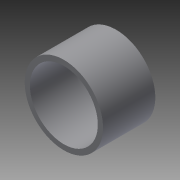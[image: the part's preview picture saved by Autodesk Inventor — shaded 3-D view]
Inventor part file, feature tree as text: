
AUTODESK INVENTOR PART (.ipt)
format: ipt  version: 2015 (Build 190159000, 159)  size: 107,008 bytes
history: native  units: mm
features: extrude x2, sketch x2
ambient origin geometry x8: Origin, YZ Plane, XZ Plane, XY Plane, X Axis, Y Axis, Z Axis, Center Point
bodies: Solid1 (feature_tree)
feature tree (4):
  extrude  "Extrusion1"  Depth=26.0mm
  extrude  "Extrusion2"  Depth=3.0mm
  sketch  "Sketch1"  dims[d0=30.0mm d1=26.0mm]
  sketch  "Sketch2"  dims[d2=20.0mm d3=0.0mm d4=28.0mm d5=26.0mm d6=3.0mm d7=0.0mm]
